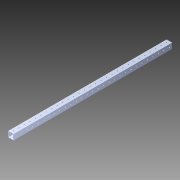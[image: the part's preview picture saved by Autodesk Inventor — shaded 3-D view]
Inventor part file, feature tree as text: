
AUTODESK INVENTOR PART (.ipt)
format: ipt  version: 2014 SP1 (Build 180222100, 222)  size: 1,259,520 bytes
history: native  units: in
note: dims shown in document units (in); Inventor stores cm internally (conversion verified against a paired STEP export)
features: pattern_circular x1, other x1, extrude x1, imported_body x1, sketch x1
ambient origin geometry x8: Origin, YZ Plane, XZ Plane, XY Plane, X Axis, Y Axis, Z Axis, Center Point
bodies: Body1 (feature_tree)
feature tree (5):
  pattern_circular  "CirPattern2"
  other  "1x1 tube1"
  extrude  "Extrusion1"  [1 undecoded]
  imported_body  "Base1"
  sketch  "Sketch1"  dims[d0=30.0in d1=0.0in]
note: 1 required parameter value undecoded (feature->parameter linkage not recoverable at this tier; creation-order binding heuristic only, values carry confidence <= 0.55)
